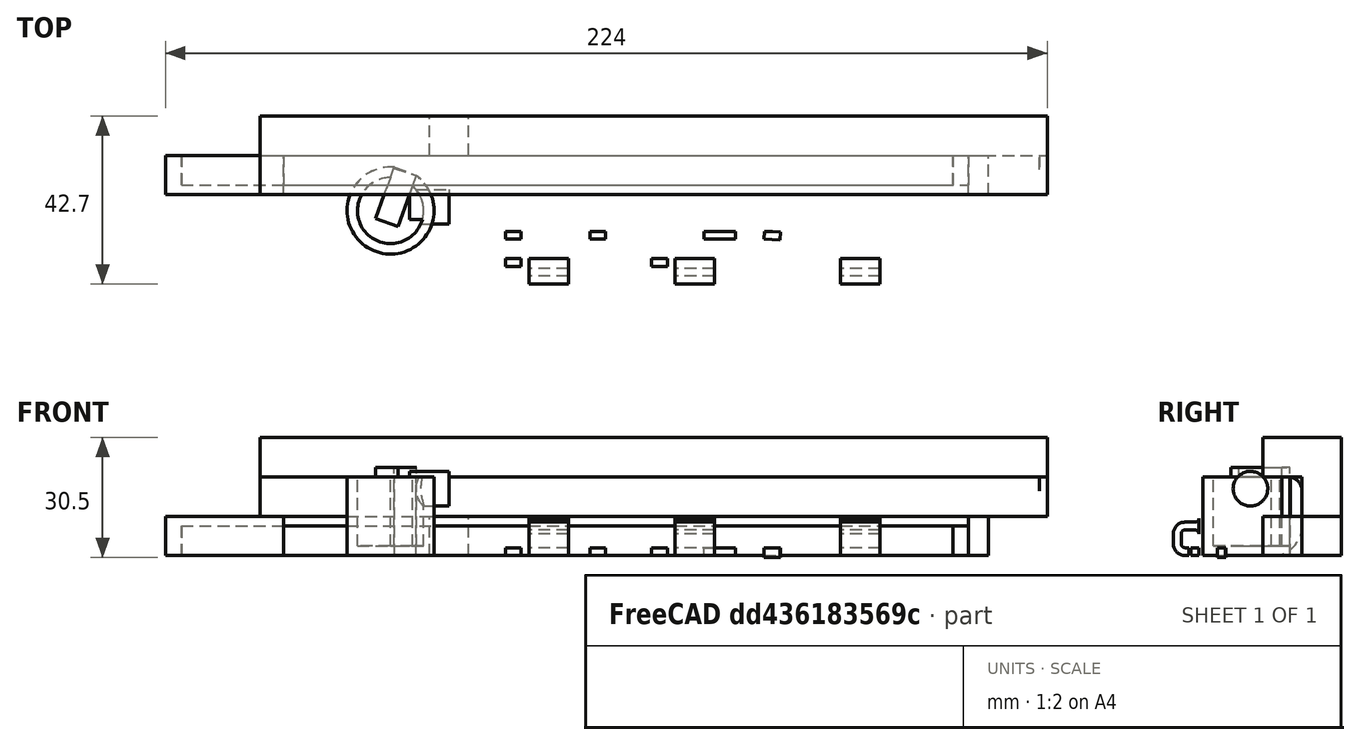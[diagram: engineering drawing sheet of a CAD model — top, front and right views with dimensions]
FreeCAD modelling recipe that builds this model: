
FCSTD DOCUMENT  (FreeCAD 0.19R0.19.2)
Label: v0_73
License: All rights reserved
LicenseURL: http://en.wikipedia.org/wiki/All_rights_reserved
objects: Part::Box×54, Part::Fillet×31, Part::MultiFuse×24, Part::Cut×13, Sketcher::SketchObject×11, Part::Extrusion×9, Part::Cylinder×6, App::MeasureDistance×5, Part::Revolution×1
note: 149 computed .brp shape members not serialized (recipe doc carries the construction recipe); baked Part::Feature solids carry a one-line shape summary decoded from their .brp

FEATURE [Sketcher::SketchObject] Sketch001
  FullyConstrained = true
  sketch-geometry (47):
    g0: Circle CenterX=-129.5 CenterY=-8 CenterZ=0 NormalX=0 NormalY=0 NormalZ=1 AngleXU=0 Radius=1
    g1: Circle CenterX=-129.5 CenterY=-3 CenterZ=0 NormalX=0 NormalY=0 NormalZ=1 AngleXU=0 Radius=1
    g2: Circle CenterX=-124.5 CenterY=-3 CenterZ=0 NormalX=0 NormalY=0 NormalZ=1 AngleXU=0 Radius=1
    g3: BSplineCurve PolesCount=3 KnotsCount=2 Degree=2 IsPeriodic=0
    g4: GeomPoint X=-129.5 Y=-8 Z=0
    g5: GeomPoint X=-124.5 Y=-3 Z=0
    g6: LineSegment StartX=18.6 StartY=-2.9 StartZ=0 EndX=23.6 EndY=-2.9 EndZ=0
    g7: ArcOfCircle CenterX=23.8 CenterY=-14.35 CenterZ=0 NormalX=0 NormalY=0 NormalZ=1 AngleXU=0 Radius=2.3 StartAngle=8e-16 EndAngle=1.5708
    g8: ArcOfCircle CenterX=23.8 CenterY=-18.1 CenterZ=0 NormalX=0 NormalY=0 NormalZ=1 AngleXU=0 Radius=2.3 StartAngle=4.71239 EndAngle=6.28319
    g9: LineSegment StartX=23.8 StartY=-20.4 StartZ=0 EndX=21.1 EndY=-20.4 EndZ=0
    g10: LineSegment StartX=21.1 StartY=-22.9 StartZ=0 EndX=21.1 EndY=-20.4 EndZ=0
    g11: LineSegment StartX=26.1 StartY=-14.35 StartZ=0 EndX=26.1 EndY=-18.1 EndZ=0
    g12: LineSegment StartX=18.6 StartY=-5.40742 StartZ=0 EndX=18.6 EndY=-2.9 EndZ=0
    g13: ArcOfCircle CenterX=18.8 CenterY=-8.1 CenterZ=0 NormalX=0 NormalY=0 NormalZ=1 AngleXU=0 Radius=2.7 StartAngle=1.64494 EndAngle=3.14159
    g14: ArcOfCircle CenterX=18.8 CenterY=-11.85 CenterZ=0 NormalX=0 NormalY=0 NormalZ=1 AngleXU=0 Radius=2.7 StartAngle=3.14159 EndAngle=4.71239
    g15: LineSegment StartX=16.1 StartY=-8.1 StartZ=0 EndX=16.1 EndY=-11.85 EndZ=0
    g16: LineSegment StartX=18.8 StartY=-14.55 StartZ=0 EndX=21.5 EndY=-14.55 EndZ=0
    g17: LineSegment StartX=21.5 StartY=-12.05 StartZ=0 EndX=21.5 EndY=-14.55 EndZ=0
    g18: LineSegment StartX=21.5 StartY=-12.05 StartZ=0 EndX=23.8 EndY=-12.05 EndZ=0
    g19: LineSegment StartX=16.1 StartY=-22.9 StartZ=0 EndX=21.1 EndY=-22.9 EndZ=0
    g20: LineSegment StartX=23.6 StartY=-2.9 StartZ=0 EndX=23.6 EndY=0 EndZ=0
    g21: LineSegment StartX=16.1 StartY=-22.9 StartZ=0 EndX=16.1 EndY=-26.2 EndZ=0
    g22: BSplineCurve PolesCount=3 KnotsCount=2 Degree=2 IsPeriodic=0
    g23: LineSegment StartX=2.6 StartY=-3 StartZ=0 EndX=-124.5 EndY=-3 EndZ=0
    g24: ArcOfCircle CenterX=-134.9 CenterY=-8.6 CenterZ=0 NormalX=0 NormalY=0 NormalZ=1 AngleXU=0 Radius=0.5 StartAngle=4.71238 EndAngle=6.28319
    g25: LineSegment StartX=-141.9 StartY=-9.1 StartZ=0 EndX=-134.9 EndY=-9.1 EndZ=0
    g26: LineSegment StartX=-141.9 StartY=-33.8 StartZ=0 EndX=-141.5 EndY=-33.8 EndZ=0
    g27: LineSegment StartX=-141.9 StartY=-9.1 StartZ=0 EndX=-141.9 EndY=-33.8 EndZ=0
    g28: LineSegment StartX=-134.4 StartY=-8.6 StartZ=0 EndX=-134.4 EndY=0 EndZ=0
    g29: LineSegment StartX=-134.4 StartY=0 StartZ=0 EndX=23.6 EndY=0 EndZ=0
    g30: LineSegment StartX=-133.5 StartY=-26.2 StartZ=0 EndX=16.1 EndY=-26.2 EndZ=0
    g31-g36: Circle x6 (B-spline internal-alignment scaffolding for g37; pole/knot coordinates omitted)
    g37: BSplineCurve PolesCount=6 KnotsCount=4 Degree=3 IsPeriodic=0
    g38-g41: GeomPoint x4 (B-spline internal-alignment scaffolding for g37; pole/knot coordinates omitted)
    g42: BSplineCurve PolesCount=3 KnotsCount=2 Degree=2 IsPeriodic=0
    g43: LineSegment StartX=-129.5 StartY=-8 StartZ=0 EndX=-129.5 EndY=-18.2 EndZ=0
    g44: BSplineCurve PolesCount=3 KnotsCount=2 Degree=2 IsPeriodic=0
    g45: LineSegment StartX=7.6 StartY=-8 StartZ=0 EndX=7.6 EndY=-18.2 EndZ=0
    g46: LineSegment StartX=2.6 StartY=-23.2 StartZ=0 EndX=-124.5 EndY=-23.2 EndZ=0
  constraints (87):
    c: Weight(g0) = 1
    c: Equal(g0,g1)
    c: Equal(g0,g2)
    c: InternalAlignment(g0,g3)
    c: InternalAlignment(g1,g3)
    c: InternalAlignment(g2,g3)
    c: InternalAlignment(g4,g3)
    c: InternalAlignment(g5,g3)
    c: Block(g3)
    c: Block(g8)
    c: Block(g7)
    c: Coincident(g9,g8)
    c: Horizontal(g9)
    c: Vertical(g10)
    c: Coincident(g10,g9)
    c: Coincident(g11,g7)
    c: Coincident(g11,g8)
    c: Vertical(g11)
    c: Vertical(g12)
    c: Block(g12)
    c: Coincident(g6,g12)
    c: Horizontal(g6)
    c: Block(g6)
    c: Coincident(g13,g12)
    c: Block(g14)
    c: Vertical(g15)
    c: Block(g15)
    c: Coincident(g16,g14)
    c: Horizontal(g16)
    c: Vertical(g17)
    c: Coincident(g17,g16)
    c: Block(g17)
    c: Coincident(g18,g7)
    c: Horizontal(g18)
    c: Block(g18)
    c: Coincident(g19,g10)
    c: Horizontal(g19)
    c: Block(g19)
    c: Block(g13)
    c: Coincident(g20,g6)
    c: Vertical(g20)
    c: Vertical(g21)
    c: Block(g21)
    c: Block(g22)
    c: Coincident(g23,g22)
    c: Coincident(g23,g3)
    c: Horizontal(g23)
    c: Block(g24)
    c: Coincident(g25,g24)
    c: Horizontal(g25)
    c: Horizontal(g26)
    c: Block(g26)
    c: Coincident(g27,g25)
    c: Coincident(g27,g26)
    c: Vertical(g27)
    c: Coincident(g28,g24)
    c: Vertical(g28)
    c: Coincident(g29,g28)
    c: Coincident(g29,g20)
    c: Horizontal(g29)
    c: Block(g29)
    c: Block(g25)
    c: Block(g28)
    c: Block(g27)
    c: Coincident(g30,g21)
    c: Horizontal(g30)
    c: Block(g30)
    c: Coincident(g37,g26)
    c: Weight(g31) = 1
    c: Equal(g31, g32-g36) x5
    c: Coincident(g37,g30)
    c: InternalAlignment(g31-g36 -> g37) x6
    c: InternalAlignment(g38-g41 -> g37) x4
    c: Block(g37)
    c: Block(g42)
    c: Coincident(g43,g3)
    c: Coincident(g43,g42)
    c: Vertical(g43)
    c: Distance(g43) = 10.2
    c: Block(g44)
    c: Coincident(g45,g22)
    c: Coincident(g45,g44)
    c: Vertical(g45)
    c: Distance(g45) = 10.2
    c: Coincident(g46,g44)
    c: Coincident(g46,g42)
    c: Horizontal(g46)
FEATURE [Part::Extrusion] Extrude001
  Base = -> Sketch001
  Dir = (0,0,1)
  DirMode = 2
  FaceMakerClass = Part::FaceMakerBullseye
  LengthFwd = 20
  LengthRev = 0
  Solid = true
  Symmetric = false
FEATURE [Sketcher::SketchObject] Sketch004
  FullyConstrained = true
  Placement = pos=(0,0,0) rot=(1,0,0;1.5708rad)
  sketch-geometry (12):
    g0: LineSegment StartX=15.75 StartY=2.5 StartZ=0 EndX=15.75 EndY=0 EndZ=0
    g1: Circle CenterX=15.75 CenterY=2.5 CenterZ=0 NormalX=0 NormalY=0 NormalZ=1 AngleXU=0 Radius=1
    g2: Circle CenterX=10.55 CenterY=2.5 CenterZ=0 NormalX=0 NormalY=0 NormalZ=1 AngleXU=0 Radius=1
    g3: Circle CenterX=10.55 CenterY=8 CenterZ=0 NormalX=0 NormalY=0 NormalZ=1 AngleXU=0 Radius=1
    g4: BSplineCurve PolesCount=3 KnotsCount=2 Degree=2 IsPeriodic=0
    g5: GeomPoint X=15.75 Y=2.5 Z=0
    g6: GeomPoint X=10.55 Y=8 Z=0
    g7: LineSegment StartX=1.9 StartY=8 StartZ=0 EndX=10.55 EndY=8 EndZ=0
    g8: LineSegment StartX=1.9 StartY=-2.4 StartZ=0 EndX=1.9 EndY=8 EndZ=0
    g9: LineSegment StartX=3.30092 StartY=-2.4 StartZ=0 EndX=3.30092 EndY=0 EndZ=0
    g10: LineSegment StartX=15.75 StartY=0 StartZ=0 EndX=3.30092 EndY=0 EndZ=0
    g11: LineSegment StartX=3.30092 StartY=-2.4 StartZ=0 EndX=1.9 EndY=-2.4 EndZ=0
  constraints (26):
    c: Vertical(g0)
    c: Distance(g0) = 2.5
    c: Coincident(g4,g0)
    c: Weight(g1) = 1
    c: Equal(g1,g2)
    c: Equal(g1,g3)
    c: InternalAlignment(g1,g4)
    c: InternalAlignment(g2,g4)
    c: InternalAlignment(g3,g4)
    c: InternalAlignment(g5,g4)
    c: InternalAlignment(g6,g4)
    c: Block(g4)
    c: Coincident(g7,g4)
    c: Horizontal(g7)
    c: Vertical(g8)
    c: Coincident(g8,g7)
    c: Block(g8)
    c: Vertical(g9)
    c: Coincident(g10,g0)
    c: PointOnObject(g10,g-1)
    c: Horizontal(g10)
    c: Coincident(g10,g9)
    c: Block(g9)
    c: Coincident(g11,g9)
    c: Coincident(g11,g8)
    c: Horizontal(g11)
FEATURE [Part::Revolution] Revolve  label="mainScrewStandRevolve"
  Angle = 360
  Axis = (0,0,1)
  Base = (0,0,0)
  FaceMakerClass = Part::FaceMakerBullseye
  Placement = pos=(-101.95,-15.3,0) rot=(0,0,1;0rad)
  Solid = true
  Source = -> Sketch004
  Symmetric = false
FEATURE [Sketcher::SketchObject] Sketch044
  FullyConstrained = true
  MapMode = 4
  Placement = pos=(0,0,0) rot=(0.57735,0.57735,0.57735;2.0944rad)
  sketch-geometry (14):
    g0: LineSegment StartX=6.08745 StartY=-4.11588 StartZ=0 EndX=6.08745 EndY=-2.11589 EndZ=0
    g1: LineSegment StartX=8.08745 StartY=1.38411 StartZ=0 EndX=8.08745 EndY=-1.11589 EndZ=0
    g2: ArcOfCircle CenterX=7.08745 CenterY=-1.11589 CenterZ=0 NormalX=0 NormalY=0 NormalZ=1 AngleXU=0 Radius=1 StartAngle=4.71239 EndAngle=6.28319
    g3: LineSegment StartX=6.08745 StartY=-2.11589 StartZ=0 EndX=7.08745 EndY=-2.11589 EndZ=0
    g4: LineSegment StartX=6.08745 StartY=-4.11588 StartZ=0 EndX=7.08745 EndY=-4.11588 EndZ=0
    g5: ArcOfCircle CenterX=7.08745 CenterY=-1.11589 CenterZ=0 NormalX=0 NormalY=0 NormalZ=1 AngleXU=0 Radius=3 StartAngle=4.71239 EndAngle=6.28319
    g6: ArcOfCircle CenterX=7.08745 CenterY=1.38411 CenterZ=0 NormalX=0 NormalY=0 NormalZ=1 AngleXU=0 Radius=1 StartAngle=5.35e-14 EndAngle=1.5708
    g7: LineSegment StartX=10.0875 StartY=-1.11588 StartZ=0 EndX=10.0875 EndY=1.38411 EndZ=0
    g8: ArcOfCircle CenterX=7.08745 CenterY=1.38411 CenterZ=0 NormalX=0 NormalY=0 NormalZ=1 AngleXU=0 Radius=3 StartAngle=3.57e-14 EndAngle=1.5708
    g9: ArcOfCircle CenterX=4.58745 CenterY=1.38412 CenterZ=0 NormalX=0 NormalY=0 NormalZ=1 AngleXU=0 Radius=1 StartAngle=1.57081 EndAngle=3.14159
    g10: LineSegment StartX=4.58744 StartY=2.38411 StartZ=0 EndX=7.08745 EndY=2.38411 EndZ=0
    g11: LineSegment StartX=4.58745 StartY=4.38411 StartZ=0 EndX=7.08745 EndY=4.38411 EndZ=0
    g12: ArcOfCircle CenterX=4.58745 CenterY=5.38411 CenterZ=0 NormalX=0 NormalY=0 NormalZ=1 AngleXU=0 Radius=1 StartAngle=3.14159 EndAngle=4.71239
    g13: LineSegment StartX=3.58745 StartY=5.38411 StartZ=0 EndX=3.58745 EndY=1.38411 EndZ=0
  constraints (33):
    c: Vertical(g0)
    c: Block(g0)
    c: Block(g1)
    c: Coincident(g2,g1)
    c: Coincident(g3,g0)
    c: Coincident(g3,g2)
    c: Horizontal(g3)
    c: Block(g2)
    c: Coincident(g4,g0)
    c: Horizontal(g4)
    c: Coincident(g5,g2)
    c: Block(g5)
    c: Block(g4)
    c: Coincident(g6,g1)
    c: Block(g6)
    c: Coincident(g7,g5)
    c: Vertical(g7)
    c: Coincident(g8,g6)
    c: Block(g8)
    c: Block(g7)
    c: Coincident(g10,g9)
    c: Coincident(g10,g6)
    c: Horizontal(g10)
    c: Block(g10)
    c: Block(g9)
    c: Coincident(g11,g8)
    c: Horizontal(g11)
    c: Block(g12)
    c: Block(g11)
    c: Coincident(g13,g12)
    c: Coincident(g13,g9)
    c: Vertical(g13)
    c: Tangent(g13,g9)
FEATURE [Sketcher::SketchObject] Sketch045
  FullyConstrained = true
  MapMode = 4
  Placement = pos=(0,0,0) rot=(0.57735,0.57735,0.57735;2.0944rad)
  sketch-geometry (14):
    g0: LineSegment StartX=6.08745 StartY=-4.11588 StartZ=0 EndX=6.08745 EndY=-2.11589 EndZ=0
    g1: LineSegment StartX=8.08745 StartY=1.38411 StartZ=0 EndX=8.08745 EndY=-1.11589 EndZ=0
    g2: ArcOfCircle CenterX=7.08745 CenterY=-1.11589 CenterZ=0 NormalX=0 NormalY=0 NormalZ=1 AngleXU=0 Radius=1 StartAngle=4.71239 EndAngle=6.28319
    g3: LineSegment StartX=6.08745 StartY=-2.11589 StartZ=0 EndX=7.08745 EndY=-2.11589 EndZ=0
    g4: LineSegment StartX=6.08745 StartY=-4.11588 StartZ=0 EndX=7.08745 EndY=-4.11588 EndZ=0
    g5: ArcOfCircle CenterX=7.08745 CenterY=-1.11589 CenterZ=0 NormalX=0 NormalY=0 NormalZ=1 AngleXU=0 Radius=3 StartAngle=4.71239 EndAngle=6.28319
    g6: ArcOfCircle CenterX=7.08745 CenterY=1.38411 CenterZ=0 NormalX=0 NormalY=0 NormalZ=1 AngleXU=0 Radius=1 StartAngle=5.35e-14 EndAngle=1.5708
    g7: LineSegment StartX=10.0875 StartY=-1.11588 StartZ=0 EndX=10.0875 EndY=1.38411 EndZ=0
    g8: ArcOfCircle CenterX=7.08745 CenterY=1.38411 CenterZ=0 NormalX=0 NormalY=0 NormalZ=1 AngleXU=0 Radius=3 StartAngle=3.57e-14 EndAngle=1.5708
    g9: ArcOfCircle CenterX=4.58745 CenterY=1.38412 CenterZ=0 NormalX=0 NormalY=0 NormalZ=1 AngleXU=0 Radius=1 StartAngle=1.57081 EndAngle=3.14159
    g10: LineSegment StartX=4.58744 StartY=2.38411 StartZ=0 EndX=7.08745 EndY=2.38411 EndZ=0
    g11: LineSegment StartX=4.58745 StartY=4.38411 StartZ=0 EndX=7.08745 EndY=4.38411 EndZ=0
    g12: ArcOfCircle CenterX=4.58745 CenterY=5.38411 CenterZ=0 NormalX=0 NormalY=0 NormalZ=1 AngleXU=0 Radius=1 StartAngle=3.14159 EndAngle=4.71239
    g13: LineSegment StartX=3.58745 StartY=5.38411 StartZ=0 EndX=3.58745 EndY=1.38411 EndZ=0
  constraints (33):
    c: Vertical(g0)
    c: Block(g0)
    c: Block(g1)
    c: Coincident(g2,g1)
    c: Coincident(g3,g0)
    c: Coincident(g3,g2)
    c: Horizontal(g3)
    c: Block(g2)
    c: Coincident(g4,g0)
    c: Horizontal(g4)
    c: Coincident(g5,g2)
    c: Block(g5)
    c: Block(g4)
    c: Coincident(g6,g1)
    c: Block(g6)
    c: Coincident(g7,g5)
    c: Vertical(g7)
    c: Coincident(g8,g6)
    c: Block(g8)
    c: Block(g7)
    c: Coincident(g10,g9)
    c: Coincident(g10,g6)
    c: Horizontal(g10)
    c: Block(g10)
    c: Block(g9)
    c: Coincident(g11,g8)
    c: Horizontal(g11)
    c: Block(g12)
    c: Block(g11)
    c: Coincident(g13,g12)
    c: Coincident(g13,g9)
    c: Vertical(g13)
    c: Tangent(g13,g9)
FEATURE [Part::Extrusion] Extrude040
  Base = -> Sketch045
  Dir = (1,0,0)
  DirMode = 2
  FaceMakerClass = Part::FaceMakerBullseye
  LengthFwd = 10
  LengthRev = 0
  Placement = pos=(-71.7,-22.61,4.115) rot=(0,0,1;3.14159rad)
  Solid = true
  Symmetric = false
FEATURE [Part::Box] Box017  label="Cube017"
  AttacherType = Attacher::AttachEngine3D
  Height = 2
  Length = 2
  Placement = pos=(-85.7,-21.3,0) rot=(0,0,1;0rad)
  Width = 2
FEATURE [Part::Box] Box018  label="Cube018"
  AttacherType = Attacher::AttachEngine3D
  Height = 2
  Length = 2
  Placement = pos=(-87.7,-21.3,0) rot=(0,0,1;0rad)
  Width = 2
FEATURE [Part::MultiFuse] Fusion
  Placement = pos=(0,-6.9,0) rot=(0,0,1;0rad)
  Shapes = -> [Box017,Box018]
FEATURE [Part::Box] Box021  label="Cube021"
  AttacherType = Attacher::AttachEngine3D
  Height = 2
  Length = 2
  Placement = pos=(-85.7,-21.3,0) rot=(0,0,1;0rad)
  Width = 2
FEATURE [Part::Box] Box022  label="Cube022"
  AttacherType = Attacher::AttachEngine3D
  Height = 2
  Length = 2
  Placement = pos=(-87.7,-21.3,0) rot=(0,0,1;0rad)
  Width = 2
FEATURE [Part::Box] Box023  label="Cube023"
  AttacherType = Attacher::AttachEngine3D
  Height = 2
  Length = 2
  Placement = pos=(-85.7,-21.3,0) rot=(0,0,1;0rad)
  Width = 2
FEATURE [Part::Box] Box024  label="Cube024"
  AttacherType = Attacher::AttachEngine3D
  Height = 2
  Length = 2
  Placement = pos=(-87.7,-21.3,0) rot=(0,0,1;0rad)
  Width = 2
FEATURE [Part::Box] Box026  label="Cube026"
  AttacherType = Attacher::AttachEngine3D
  Height = 2
  Length = 2
  Placement = pos=(-87.7,-21.3,0) rot=(0,0,1;0rad)
  Width = 2
FEATURE [Part::Box] Box  label="Cube"
  AttacherType = Attacher::AttachEngine3D
  Height = 10
  Length = 10
  Placement = pos=(-107,0,0) rot=(0,0,1;0rad)
  Width = 10
FEATURE [Sketcher::SketchObject] Sketch046
  FullyConstrained = true
  MapMode = 4
  Placement = pos=(0,0,0) rot=(0.57735,0.57735,0.57735;2.0944rad)
  sketch-geometry (14):
    g0: LineSegment StartX=6.08745 StartY=-4.11588 StartZ=0 EndX=6.08745 EndY=-2.11589 EndZ=0
    g1: LineSegment StartX=8.08745 StartY=1.38411 StartZ=0 EndX=8.08745 EndY=-1.11589 EndZ=0
    g2: ArcOfCircle CenterX=7.08745 CenterY=-1.11589 CenterZ=0 NormalX=0 NormalY=0 NormalZ=1 AngleXU=0 Radius=1 StartAngle=4.71239 EndAngle=6.28319
    g3: LineSegment StartX=6.08745 StartY=-2.11589 StartZ=0 EndX=7.08745 EndY=-2.11589 EndZ=0
    g4: LineSegment StartX=6.08745 StartY=-4.11588 StartZ=0 EndX=7.08745 EndY=-4.11588 EndZ=0
    g5: ArcOfCircle CenterX=7.08745 CenterY=-1.11589 CenterZ=0 NormalX=0 NormalY=0 NormalZ=1 AngleXU=0 Radius=3 StartAngle=4.71239 EndAngle=6.28319
    g6: ArcOfCircle CenterX=7.08745 CenterY=1.38411 CenterZ=0 NormalX=0 NormalY=0 NormalZ=1 AngleXU=0 Radius=1 StartAngle=5.35e-14 EndAngle=1.5708
    g7: LineSegment StartX=10.0875 StartY=-1.11588 StartZ=0 EndX=10.0875 EndY=1.38411 EndZ=0
    g8: ArcOfCircle CenterX=7.08745 CenterY=1.38411 CenterZ=0 NormalX=0 NormalY=0 NormalZ=1 AngleXU=0 Radius=3 StartAngle=3.57e-14 EndAngle=1.5708
    g9: ArcOfCircle CenterX=4.58745 CenterY=1.38412 CenterZ=0 NormalX=0 NormalY=0 NormalZ=1 AngleXU=0 Radius=1 StartAngle=1.57081 EndAngle=3.14159
    g10: LineSegment StartX=4.58744 StartY=2.38411 StartZ=0 EndX=7.08745 EndY=2.38411 EndZ=0
    g11: LineSegment StartX=4.58745 StartY=4.38411 StartZ=0 EndX=7.08745 EndY=4.38411 EndZ=0
    g12: ArcOfCircle CenterX=4.58745 CenterY=5.38411 CenterZ=0 NormalX=0 NormalY=0 NormalZ=1 AngleXU=0 Radius=1 StartAngle=3.14159 EndAngle=4.71239
    g13: LineSegment StartX=3.58745 StartY=5.38411 StartZ=0 EndX=3.58745 EndY=1.38411 EndZ=0
  constraints (33):
    c: Vertical(g0)
    c: Block(g0)
    c: Block(g1)
    c: Coincident(g2,g1)
    c: Coincident(g3,g0)
    c: Coincident(g3,g2)
    c: Horizontal(g3)
    c: Block(g2)
    c: Coincident(g4,g0)
    c: Horizontal(g4)
    c: Coincident(g5,g2)
    c: Block(g5)
    c: Block(g4)
    c: Coincident(g6,g1)
    c: Block(g6)
    c: Coincident(g7,g5)
    c: Vertical(g7)
    c: Coincident(g8,g6)
    c: Block(g8)
    c: Block(g7)
    c: Coincident(g10,g9)
    c: Coincident(g10,g6)
    c: Horizontal(g10)
    c: Block(g10)
    c: Block(g9)
    c: Coincident(g11,g8)
    c: Horizontal(g11)
    c: Block(g12)
    c: Block(g11)
    c: Coincident(g13,g12)
    c: Coincident(g13,g9)
    c: Vertical(g13)
    c: Tangent(g13,g9)
FEATURE [Part::Extrusion] Extrude041
  Base = -> Sketch046
  Dir = (1,0,0)
  DirMode = 2
  FaceMakerClass = Part::FaceMakerBullseye
  LengthFwd = 10
  LengthRev = 0
  Placement = pos=(7.5,-22.61,4.115) rot=(0,0,1;3.14159rad)
  Solid = true
  Symmetric = false
FEATURE [Part::Box] Box027  label="Cube027"
  AttacherType = Attacher::AttachEngine3D
  Height = 2
  Length = 2
  Placement = pos=(-85.7,-21.3,0) rot=(0,0,1;0rad)
  Width = 2
FEATURE [Part::Box] Box028  label="Cube028"
  AttacherType = Attacher::AttachEngine3D
  Height = 2
  Length = 2
  Placement = pos=(-87.7,-21.3,0) rot=(0,0,1;0rad)
  Width = 2
FEATURE [Part::MultiFuse] Fusion009
  Placement = pos=(21.5,0,0) rot=(0,0,1;0rad)
  Shapes = -> [Box027,Box028]
FEATURE [Part::Box] Box029  label="Cube029"
  AttacherType = Attacher::AttachEngine3D
  Height = 2
  Length = 2
  Placement = pos=(-87.7,-21.3,0) rot=(0,0,1;0rad)
  Width = 2
FEATURE [Part::Box] Box030  label="Cube030"
  AttacherType = Attacher::AttachEngine3D
  Height = 2
  Length = 2
  Placement = pos=(-85.7,-21.3,0) rot=(0,0,1;0rad)
  Width = 2
FEATURE [Part::MultiFuse] Fusion010
  Shapes = -> [Box030,Box029]
FEATURE [Part::Box] Box032  label="Cube032"
  AttacherType = Attacher::AttachEngine3D
  Height = 2
  Length = 2
  Placement = pos=(-85.7,-21.3,0) rot=(0,0,1;0rad)
  Width = 2
FEATURE [Part::Box] Box033  label="Cube033"
  AttacherType = Attacher::AttachEngine3D
  Height = 2
  Length = 2
  Placement = pos=(-87.7,-21.3,0) rot=(0,0,1;0rad)
  Width = 2
FEATURE [Part::MultiFuse] Fusion011
  Shapes = -> [Box032,Box033]
FEATURE [Part::Box] Box042  label="Cube042"
  AttacherType = Attacher::AttachEngine3D
  Height = 2
  Length = 2
  Placement = pos=(-87.7,-21.3,0) rot=(0,0,1;0rad)
  Width = 2
FEATURE [Part::Box] Box043  label="Cube043"
  AttacherType = Attacher::AttachEngine3D
  Height = 2
  Length = 2
  Placement = pos=(-85.7,-21.3,0) rot=(0,0,1;0rad)
  Width = 2
FEATURE [Part::MultiFuse] Fusion019
  Placement = pos=(37.15,-6.9,0) rot=(0,0,1;0rad)
  Shapes = -> [Box043,Box042]
FEATURE [Part::Box] Box044  label="Cube044"
  AttacherType = Attacher::AttachEngine3D
  Height = 2
  Length = 2
  Placement = pos=(-87.7,-21.3,0) rot=(0,0,1;0rad)
  Width = 2
FEATURE [Part::Box] Box045  label="Cube045"
  AttacherType = Attacher::AttachEngine3D
  Height = 2
  Length = 2
  Placement = pos=(-85.7,-21.3,0) rot=(0,0,1;0rad)
  Width = 2
FEATURE [Part::MultiFuse] Fusion020
  Placement = pos=(69.3,0,0) rot=(0,0,1;0rad)
  Shapes = -> [Box045,Box044]
FEATURE [Part::Box] Box046  label="Cube046"
  AttacherType = Attacher::AttachEngine3D
  Height = 2
  Length = 2
  Placement = pos=(-87.7,-21.3,0) rot=(0,0,1;0rad)
  Width = 2
FEATURE [Part::Box] Box047  label="Cube047"
  AttacherType = Attacher::AttachEngine3D
  Height = 2
  Length = 2
  Placement = pos=(-85.7,-21.3,0) rot=(0,0,1;0rad)
  Width = 2
FEATURE [Part::MultiFuse] Fusion021
  Placement = pos=(73.3,0,0) rot=(0,0,1;0rad)
  Shapes = -> [Box047,Box046]
FEATURE [Part::Box] Box048  label="Cube048"
  AttacherType = Attacher::AttachEngine3D
  Height = 2
  Length = 2
  Placement = pos=(-87.7,-21.3,0) rot=(0,0,1;0rad)
  Width = 2
FEATURE [Part::Box] Box049  label="Cube049"
  AttacherType = Attacher::AttachEngine3D
  Height = 2
  Length = 2
  Placement = pos=(-85.7,-21.3,0) rot=(0,0,1;0rad)
  Width = 2
FEATURE [Part::MultiFuse] Fusion022
  Placement = pos=(64.3,0,0) rot=(0,0,1;0rad)
  Shapes = -> [Box049,Box048]
FEATURE [Part::MultiFuse] Fusion025
  Shapes = -> [Box021,Box022,Box023,Box024,Box026]
FEATURE [Part::Box] Box005  label="Cube005"
  AttacherType = Attacher::AttachEngine3D
  Height = 10
  Length = 198
  Placement = pos=(-30,0,0) rot=(0,0,1;0rad)
  Width = 10
FEATURE [Part::Box] Box004  label="Cube004"
  AttacherType = Attacher::AttachEngine3D
  Height = 10
  Length = 200
  Placement = pos=(-30,0,0) rot=(0,0,1;0rad)
  Width = 10
FEATURE [Part::Fillet] Fillet020
  Base = -> Box004
  Edges = 1 edges r=3.6: [Edge12]
FEATURE [Sketcher::SketchObject] Sketch
  FullyConstrained = true
  sketch-geometry (35):
    g0: Circle CenterX=-101.95 CenterY=-14.3 CenterZ=0 NormalX=0 NormalY=0 NormalZ=1 AngleXU=0 Radius=3.25
    g1: LineSegment StartX=16.1 StartY=-26.2 StartZ=0 EndX=16.1 EndY=-22.9 EndZ=0
    g2: ArcOfCircle CenterX=23.8 CenterY=-14.35 CenterZ=0 NormalX=0 NormalY=0 NormalZ=1 AngleXU=0 Radius=2.3 StartAngle=8e-16 EndAngle=1.5708
    g3: LineSegment StartX=18.6 StartY=-5.40742 StartZ=0 EndX=18.6 EndY=-2.9 EndZ=0
    g4: LineSegment StartX=18.6 StartY=-2.9 StartZ=0 EndX=23.6 EndY=-2.9 EndZ=0
    g5: LineSegment StartX=23.6 StartY=-2.9 StartZ=0 EndX=23.6 EndY=2.58e-14 EndZ=0
    g6: LineSegment StartX=18.8 StartY=-14.55 StartZ=0 EndX=21.5 EndY=-14.55 EndZ=0
    g7: LineSegment StartX=21.5 StartY=-12.05 StartZ=0 EndX=21.5 EndY=-14.55 EndZ=0
    g8: LineSegment StartX=21.5 StartY=-12.05 StartZ=0 EndX=23.8 EndY=-12.05 EndZ=0
    g9: ArcOfCircle CenterX=23.8 CenterY=-18.1 CenterZ=0 NormalX=0 NormalY=0 NormalZ=1 AngleXU=0 Radius=2.3 StartAngle=4.71239 EndAngle=6.28319
    g10: LineSegment StartX=23.8 StartY=-20.4 StartZ=0 EndX=21.1 EndY=-20.4 EndZ=0
    g11: LineSegment StartX=26.1 StartY=-14.35 StartZ=0 EndX=26.1 EndY=-18.1 EndZ=0
    g12: ArcOfCircle CenterX=18.8 CenterY=-8.1 CenterZ=0 NormalX=0 NormalY=0 NormalZ=1 AngleXU=0 Radius=2.7 StartAngle=1.64494 EndAngle=3.14159
    g13: ArcOfCircle CenterX=18.8 CenterY=-11.85 CenterZ=0 NormalX=0 NormalY=0 NormalZ=1 AngleXU=0 Radius=2.7 StartAngle=3.14159 EndAngle=4.71239
    g14: LineSegment StartX=16.1 StartY=-8.1 StartZ=0 EndX=16.1 EndY=-11.85 EndZ=0
    g15: LineSegment StartX=21.1 StartY=-22.9 StartZ=0 EndX=21.1 EndY=-20.4 EndZ=0
    g16: LineSegment StartX=16.1 StartY=-22.9 StartZ=0 EndX=21.1 EndY=-22.9 EndZ=0
    g17: LineSegment StartX=23.6 StartY=2.58e-14 StartZ=0 EndX=-134.4 EndY=2.58e-14 EndZ=0
    g18: LineSegment StartX=-134.4 StartY=2.59e-14 StartZ=0 EndX=-134.4 EndY=-8.6 EndZ=0
    g19: ArcOfCircle CenterX=-134.9 CenterY=-8.6 CenterZ=0 NormalX=0 NormalY=0 NormalZ=1 AngleXU=0 Radius=0.5 StartAngle=4.71238 EndAngle=6.28319
    g20: LineSegment StartX=-134.9 StartY=-9.1 StartZ=0 EndX=-141.9 EndY=-9.1 EndZ=0
    g21: LineSegment StartX=-141.9 StartY=-9.1 StartZ=0 EndX=-141.9 EndY=-33.8 EndZ=0
    g22: LineSegment StartX=-141.9 StartY=-33.8 StartZ=0 EndX=-141.5 EndY=-33.8 EndZ=0
    g23: LineSegment StartX=-133.5 StartY=-26.2 StartZ=0 EndX=16.1 EndY=-26.2 EndZ=0
    g24-g29: Circle x6 (B-spline internal-alignment scaffolding for g30; pole/knot coordinates omitted)
    g30: BSplineCurve PolesCount=6 KnotsCount=4 Degree=3 IsPeriodic=0
    g31-g34: GeomPoint x4 (B-spline internal-alignment scaffolding for g30; pole/knot coordinates omitted)
  constraints (61):
    c: Block(g0)
    c: Vertical(g1)
    c: Distance(g1) = 3.3
    c: Block(g9)
    c: Block(g2)
    c: Coincident(g10,g9)
    c: Horizontal(g10)
    c: Vertical(g15)
    c: Coincident(g15,g10)
    c: Coincident(g11,g2)
    c: Coincident(g11,g9)
    c: Vertical(g11)
    c: Vertical(g3)
    c: Block(g3)
    c: Coincident(g4,g3)
    c: Horizontal(g4)
    c: Vertical(g5)
    c: Block(g5)
    c: Block(g4)
    c: Coincident(g12,g3)
    c: Block(g13)
    c: Coincident(g14,g12)
    c: Vertical(g14)
    c: Block(g14)
    c: Coincident(g6,g13)
    c: Horizontal(g6)
    c: Vertical(g7)
    c: Coincident(g7,g6)
    c: Block(g7)
    c: Coincident(g8,g2)
    c: Horizontal(g8)
    c: Block(g8)
    c: Coincident(g16,g15)
    c: Horizontal(g16)
    c: Block(g16)
    c: Block(g12)
    c: Coincident(g16,g1)
    c: Coincident(g17,g5)
    c: Horizontal(g17)
    c: Vertical(g18)
    c: Horizontal(g20)
    c: Coincident(g19,g18)
    c: Coincident(g19,g20)
    c: Block(g19)
    c: Coincident(g21,g20)
    c: Vertical(g21)
    c: Block(g21)
    c: Coincident(g22,g21)
    c: Horizontal(g22)
    c: Block(g22)
    c: Block(g18)
    c: Coincident(g18,g17)
    c: Coincident(g23,g1)
    c: Horizontal(g23)
    c: Distance(g23) = 149.6
    c: Coincident(g30,g22)
    c: Weight(g24) = 1
    c: Equal(g24, g25-g29) x5
    c: InternalAlignment(g24-g29 -> g30) x6
    c: InternalAlignment(g31-g34 -> g30) x4
    c: Block(g30)
FEATURE [Part::Extrusion] Extrude
  Base = -> Sketch
  Dir = (0,0,1)
  DirMode = 2
  FaceMakerClass = Part::FaceMakerBullseye
  LengthFwd = 2.4
  LengthRev = 0
  Solid = true
  Symmetric = false
FEATURE [Part::Box] Box051  label="Cube051"
  AttacherType = Attacher::AttachEngine3D
  Height = 10
  Length = 198
  Placement = pos=(-30,0,0) rot=(0,0,1;0rad)
  Width = 10
FEATURE [Part::Box] Box052  label="Cube052"
  AttacherType = Attacher::AttachEngine3D
  Height = 5
  Length = 200
  Placement = pos=(-30,6.4,10) rot=(1,0,0;0rad)
  Width = 5
FEATURE [Part::Box] Box053  label="Cube053"
  AttacherType = Attacher::AttachEngine3D
  Height = 5
  Length = 200
  Placement = pos=(-30,6.4,10) rot=(1,0,0;0.872665rad)
  Width = 5
FEATURE [Part::Box] Box054  label="Cube054"
  AttacherType = Attacher::AttachEngine3D
  Height = 10
  Length = 200
  Placement = pos=(-30,0,0) rot=(0,0,1;0rad)
  Width = 10
FEATURE [Part::Fillet] Fillet021
  Base = -> Box054
  Edges = 1 edges r=3.6: [Edge12]
FEATURE [Part::Cut] Cut015
  Base = -> Box051
  Tool = -> Fillet021
FEATURE [Part::MultiFuse] Fusion033  label="removeFromMainFusion014"
  Placement = pos=(-120,-10,10) rot=(0,0,1;0rad)
  Shapes = -> [Box053,Box052,Cut015]
FEATURE [Part::Box] Box055  label="Cube055"
  AttacherType = Attacher::AttachEngine3D
  Height = 10
  Length = 190
  Placement = pos=(-30,0,0) rot=(0,0,1;0rad)
  Width = 10
FEATURE [Part::Box] Box056  label="Cube056"
  AttacherType = Attacher::AttachEngine3D
  Height = 10
  Length = 190
  Placement = pos=(-35,0,0) rot=(0,0,1;0rad)
  Width = 10
FEATURE [Part::Fillet] Fillet022
  Base = -> Box055
  Edges = 1 edges r=7.5: [Edge11]
FEATURE [Part::Cut] Cut014  label="filletMain001"
  Base = -> Box056
  Placement = pos=(-120,-10,0) rot=(0,0,1;0rad)
  Tool = -> Fillet022
FEATURE [Part::MultiFuse] Fusion032  label="removeFromMain001"
  Shapes = -> [Fusion033,Cut014]
FEATURE [Part::Cut] Cut017
  Base = -> Extrude
  Tool = -> Fusion032
FEATURE [Part::Box] Box063  label="Cube063"
  AttacherType = Attacher::AttachEngine3D
  Height = 10
  Length = 198
  Placement = pos=(-30,0,0) rot=(0,0,1;0rad)
  Width = 10
FEATURE [Part::Box] Box064  label="Cube064"
  AttacherType = Attacher::AttachEngine3D
  Height = 5
  Length = 200
  Placement = pos=(-30,6.4,10) rot=(1,0,0;0rad)
  Width = 5
FEATURE [Part::Box] Box065  label="Cube065"
  AttacherType = Attacher::AttachEngine3D
  Height = 5
  Length = 200
  Placement = pos=(-30,6.4,10) rot=(1,0,0;0.872665rad)
  Width = 5
FEATURE [Part::Box] Box066  label="Cube066"
  AttacherType = Attacher::AttachEngine3D
  Height = 10
  Length = 200
  Placement = pos=(-30,0,0) rot=(0,0,1;0rad)
  Width = 10
FEATURE [Part::Fillet] Fillet023
  Base = -> Box066
  Edges = 1 edges r=3.6: [Edge12]
FEATURE [Part::Cut] Cut018
  Base = -> Box063
  Tool = -> Fillet023
FEATURE [Part::MultiFuse] Fusion035  label="removeFromMainFusion015"
  Placement = pos=(-120,-10,10) rot=(0,0,1;0rad)
  Shapes = -> [Box065,Box064,Cut018]
FEATURE [Part::Box] Box067  label="Cube067"
  AttacherType = Attacher::AttachEngine3D
  Height = 10
  Length = 190
  Placement = pos=(-30,0,0) rot=(0,0,1;0rad)
  Width = 10
FEATURE [Part::Fillet] Fillet024
  Base = -> Box067
  Edges = 1 edges r=7.5: [Edge11]
FEATURE [Part::Box] Box068  label="Cube068"
  AttacherType = Attacher::AttachEngine3D
  Height = 10
  Length = 190
  Placement = pos=(-35,0,0) rot=(0,0,1;0rad)
  Width = 10
FEATURE [Part::Cut] Cut019  label="filletMain002"
  Base = -> Box068
  Placement = pos=(-120,-10,0) rot=(0,0,1;0rad)
  Tool = -> Fillet024
FEATURE [Part::MultiFuse] Fusion036  label="removeFromMain002"
  Shapes = -> [Fusion035,Cut019]
FEATURE [Part::Box] Box069  label="Cube069"
  AttacherType = Attacher::AttachEngine3D
  Height = 20
  Length = 10
  Placement = pos=(-144.4,-8,0) rot=(0,0,1;0rad)
  Width = 10
FEATURE [Part::Box] Box070  label="Cube070"
  AttacherType = Attacher::AttachEngine3D
  Height = 20
  Length = 30
  Placement = pos=(-120,0,0) rot=(0,0,1;0rad)
  Width = 20
FEATURE [Part::MultiFuse] Fusion037  label="removeFromIntegrityIncreaserFusion037"
  Shapes = -> [Box069,Box070,Fusion036]
FEATURE [Sketcher::SketchObject] Sketch047
  FullyConstrained = true
  sketch-geometry (4):
    g0: LineSegment StartX=20.5 StartY=-1.82002 StartZ=0 EndX=20.5 EndY=-36 EndZ=0
    g1: LineSegment StartX=32.7 StartY=-36 StartZ=0 EndX=32.7 EndY=-1.82002 EndZ=0
    g2: LineSegment StartX=20.5 StartY=-1.82002 StartZ=0 EndX=32.7 EndY=-1.82002 EndZ=0
    g3: LineSegment StartX=20.5 StartY=-36 StartZ=0 EndX=32.7 EndY=-36 EndZ=0
  constraints (12):
    c: Vertical(g0)
    c: Distance(g0) = 34.18
    c: Vertical(g1)
    c: Block(g0)
    c: Coincident(g2,g0)
    c: Horizontal(g2)
    c: Coincident(g2,g1)
    c: Block(g2)
    c: Block(g1)
    c: Coincident(g3,g0)
    c: Coincident(g3,g1)
    c: Horizontal(g3)
FEATURE [Part::MultiFuse] Fusion038
  Placement = pos=(-18.8,0,0) rot=(0,0,1;0rad)
  Shapes = -> [Fusion020,Fusion021]
FEATURE [Part::Box] Box071  label="Cube071"
  AttacherType = Attacher::AttachEngine3D
  Height = 2
  Length = 2
  Placement = pos=(-87.7,-21.3,0) rot=(0,0,1;0rad)
  Width = 2
FEATURE [Part::Box] Box072  label="Cube072"
  AttacherType = Attacher::AttachEngine3D
  Height = 2
  Length = 2
  Placement = pos=(-85.7,-21.3,0) rot=(0,0,1;0rad)
  Width = 2
FEATURE [Part::MultiFuse] Fusion039
  Placement = pos=(64.3,0,-0.5) rot=(0,0,1;0rad)
  Shapes = -> [Box072,Box071]
FEATURE [Part::MultiFuse] Fusion040  label="removeFromHook"
  Placement = pos=(2.4,-1.09,0) rot=(0,0,-1;0.045379rad)
  Shapes = -> [Fusion022,Fusion039]
FEATURE [Part::Cut] Cut021
  Base = -> Box005
  Tool = -> Fillet020
FEATURE [Part::Box] Box073  label="Cube073"
  AttacherType = Attacher::AttachEngine3D
  Height = 10
  Length = 200
  Placement = pos=(-30,10,0) rot=(0,0,1;0rad)
  Width = 10
FEATURE [Part::Box] Box074  label="Cube074"
  AttacherType = Attacher::AttachEngine3D
  Height = 10
  Length = 200
  Placement = pos=(-30,0,10) rot=(0,0,1;0rad)
  Width = 10
FEATURE [Part::Box] Box075  label="Cube075"
  AttacherType = Attacher::AttachEngine3D
  Height = 10
  Length = 200
  Placement = pos=(-30,10,10) rot=(0,0,1;0rad)
  Width = 10
FEATURE [Part::MultiFuse] Fusion043  label="removeFromMainFusion043"
  Placement = pos=(-120,-10,10) rot=(0,0,1;0rad)
  Shapes = -> [Cut021,Box074,Box073,Box075]
FEATURE [Part::Box] Box076  label="Cube076"
  AttacherType = Attacher::AttachEngine3D
  Height = 10
  Length = 200
  Placement = pos=(-160,0,0) rot=(0,0,1;0rad)
  Width = 10
FEATURE [Part::Box] Box077  label="Cube077"
  AttacherType = Attacher::AttachEngine3D
  Height = 10
  Length = 170
  Placement = pos=(-130,0,0) rot=(0,0,1;0rad)
  Width = 10
FEATURE [Part::Fillet] Fillet028
  Base = -> Box077
  Edges = 1 edges r=7.5: [Edge11]
FEATURE [Part::Cut] Cut024
  Base = -> Box076
  Placement = pos=(-14,-10,0) rot=(0,0,1;0rad)
  Tool = -> Fillet028
FEATURE [Part::Box] Box078  label="Cube078"
  AttacherType = Attacher::AttachEngine3D
  Height = 10
  Length = 200
  Width = 10
FEATURE [Part::Box] Box079  label="Cube079"
  AttacherType = Attacher::AttachEngine3D
  Height = 10
  Length = 205
  Placement = pos=(10,0,0) rot=(0,0,1;0rad)
  Width = 10
FEATURE [Part::Fillet] Fillet029
  Base = -> Box078
  Edges = 1 edges r=7.5: [Edge11]
  Placement = pos=(10,0,0) rot=(0,0,1;0rad)
FEATURE [Part::Cut] Cut025  label="removeFromMainCut025"
  Base = -> Box079
  Placement = pos=(-180,-10,0) rot=(0,0,1;0rad)
  Tool = -> Fillet029
FEATURE [Part::Cylinder] Cylinder001
  Angle = 360
  AttacherType = Attacher::AttachEngine3D
  Height = 10
  Placement = pos=(-36.2,-2,12) rot=(0,1,0;1.5708rad)
  Radius = 2
FEATURE [App::MeasureDistance] Distance  label="Distance: 4.02 mm"
  Distance = 4.02
  P1 = (-33.21,5.8978,9.90268)
  P2 = (-29.19,5.8978,9.90268)
FEATURE [Part::Fillet] Fillet030
  Base = -> Cylinder001
  Edges = 1 edges r=1.8: [Edge3]
FEATURE [Part::Fillet] Fillet031
  Base = -> Fillet030
  Edges = 1 edges r=1.8: [Edge2]
FEATURE [Part::Cylinder] Cylinder003
  Angle = 360
  AttacherType = Attacher::AttachEngine3D
  Height = 10
  Placement = pos=(-36.2,-2,12) rot=(0,1,0;1.5708rad)
  Radius = 2
FEATURE [Part::Fillet] Fillet035
  Base = -> Cylinder003
  Edges = 1 edges r=1.8: [Edge3]
FEATURE [Part::Fillet] Fillet036
  Base = -> Fillet035
  Edges = 1 edges r=1.8: [Edge2]
  Placement = pos=(-12.8,0,0) rot=(0,0,1;0rad)
FEATURE [Part::Cylinder] Cylinder004
  Angle = 360
  AttacherType = Attacher::AttachEngine3D
  Height = 10
  Placement = pos=(-36.2,-2,12) rot=(0,1,0;1.5708rad)
  Radius = 2
FEATURE [Part::Fillet] Fillet038
  Base = -> Cylinder004
  Edges = 1 edges r=1.8: [Edge3]
FEATURE [Part::Fillet] Fillet037
  Base = -> Fillet038
  Edges = 1 edges r=1.8: [Edge2]
  Placement = pos=(-6.4,0,0) rot=(0,0,1;0rad)
FEATURE [Sketcher::SketchObject] Sketch048
  FullyConstrained = true
  sketch-geometry (4):
    g0: LineSegment StartX=-5.1 StartY=-34.18 StartZ=0 EndX=5.1 EndY=-34.18 EndZ=0
    g1: LineSegment StartX=-5.1 StartY=-3.93167e-07 StartZ=0 EndX=-5.1 EndY=-34.18 EndZ=0
    g2: LineSegment StartX=5.1 StartY=-34.18 StartZ=0 EndX=5.1 EndY=-3.93167e-07 EndZ=0
    g3: LineSegment StartX=-5.1 StartY=-3.93167e-07 StartZ=0 EndX=5.1 EndY=-3.93167e-07 EndZ=0
  constraints (10):
    c: Horizontal(g0)
    c: Block(g0)
    c: Coincident(g1,g0)
    c: Vertical(g1)
    c: Coincident(g2,g0)
    c: Vertical(g2)
    c: Coincident(g3,g1)
    c: Coincident(g3,g2)
    c: Horizontal(g3)
    c: Block(g3)
FEATURE [Part::Extrusion] Extrude044
  Base = -> Sketch048
  Dir = (0,0,1)
  DirMode = 2
  FaceMakerClass = Part::FaceMakerBullseye
  LengthFwd = 6.2
  LengthRev = 0
  Solid = true
  Symmetric = false
FEATURE [Part::Fillet] Fillet039
  Base = -> Extrude044
  Edges = 1 edges r=3.09: [Edge7]
FEATURE [Part::Fillet] Fillet040
  Base = -> Fillet039
  Edges = 1 edges r=3.09: [Edge8]
FEATURE [Part::Fillet] Fillet041
  Base = -> Fillet040
  Edges = 1 edges r=3.09: [Edge17]
FEATURE [Part::Fillet] Fillet042  label="removeFromMainToMakeUSBCableHole"
  Base = -> Fillet041
  Edges = 1 edges r=3.09: [Edge10]
  Placement = pos=(-111.4,30,10.9) rot=(0,1,0;1.5708rad)
FEATURE [Part::Cylinder] Cylinder
  Angle = 360
  AttacherType = Attacher::AttachEngine3D
  Height = 17.6
  Placement = pos=(-116.86,-14.05,2.4) rot=(0,0,1;0rad)
  Radius = 8.4
FEATURE [Part::Box] Box080  label="Cube080"
  AttacherType = Attacher::AttachEngine3D
  Height = 20
  Length = 6
  Placement = pos=(-120.65,-16.05,2.4) rot=(0,0,-1;0.349066rad)
  Width = 13.85
FEATURE [Part::Cylinder] Cylinder005
  Angle = 360
  AttacherType = Attacher::AttachEngine3D
  Height = 20
  Placement = pos=(-116.86,-14.05,30) rot=(0,0,1;0rad)
  Radius = 11.06
FEATURE [Part::Box] Box081  label="Cube081"
  AttacherType = Attacher::AttachEngine3D
  Height = 20
  Length = 10
  Placement = pos=(-115.9,-3.3,30) rot=(0,0,-1;0.314159rad)
  Width = 10
FEATURE [App::MeasureDistance] Distance001  label="Distance: 2.40 mm"
  Distance = 2.4
  P1 = (-129.5,-19.3,2.4)
  P2 = (-129.5,-19.3,0)
FEATURE [Part::MultiFuse] Fusion047
  Shapes = -> [Box080,Cylinder]
FEATURE [Part::Cylinder] Cylinder006
  Angle = 360
  AttacherType = Attacher::AttachEngine3D
  Height = 10
  Placement = pos=(-112,-13.1,17) rot=(0,1,0;1.5708rad)
  Radius = 4.4
FEATURE [Part::MultiFuse] Fusion048  label="removeFromMainToCreateHoleForUSBCablePillar"
  Shapes = -> [Fusion047,Cylinder006]
FEATURE [Part::Extrusion] Extrude046
  Base = -> Sketch047
  Dir = (0,0,1)
  DirMode = 2
  FaceMakerClass = Part::FaceMakerBullseye
  LengthFwd = 8
  LengthRev = 0
  Solid = true
  Symmetric = false
FEATURE [App::MeasureDistance] Distance002  label="Distance: 12.20 mm"
  Distance = 12.2
  P1 = (32.7,-36,8)
  P2 = (20.5,-36,8)
FEATURE [Part::Fillet] Fillet
  Base = -> Extrude046
  Edges = 1 edges r=3.9: [Edge12]
FEATURE [Part::Fillet] Fillet048
  Base = -> Fillet
  Edges = 1 edges r=3.9: [Edge8]
FEATURE [Part::Fillet] Fillet049
  Base = -> Fillet048
  Edges = 1 edges r=3.9: [Edge17]
FEATURE [Part::Fillet] Fillet050
  Base = -> Fillet049
  Edges = 1 edges r=3.9: [Edge11]
  Placement = pos=(-55,0,8.3) rot=(1,0,0;0.191986rad)
FEATURE [Part::MultiFuse] Fusion049
  Shapes = -> [Fillet031,Fillet036,Fillet037]
FEATURE [Part::Cut] Cut027
  Base = -> Cylinder005
  Placement = pos=(0,0,-30) rot=(0,0,1;0rad)
  Tool = -> Box081
FEATURE [Sketcher::SketchObject] Sketch049
  FullyConstrained = true
  sketch-geometry (4):
    g0: LineSegment StartX=-5.1 StartY=-34.18 StartZ=0 EndX=5.1 EndY=-34.18 EndZ=0
    g1: LineSegment StartX=-5.1 StartY=-3.93167e-07 StartZ=0 EndX=-5.1 EndY=-34.18 EndZ=0
    g2: LineSegment StartX=5.1 StartY=-34.18 StartZ=0 EndX=5.1 EndY=-3.93167e-07 EndZ=0
    g3: LineSegment StartX=-5.1 StartY=-3.93167e-07 StartZ=0 EndX=5.1 EndY=-3.93167e-07 EndZ=0
  constraints (10):
    c: Horizontal(g0)
    c: Block(g0)
    c: Coincident(g1,g0)
    c: Vertical(g1)
    c: Coincident(g2,g0)
    c: Vertical(g2)
    c: Coincident(g3,g1)
    c: Coincident(g3,g2)
    c: Horizontal(g3)
    c: Block(g3)
FEATURE [Part::Extrusion] Extrude047
  Base = -> Sketch049
  Dir = (0,0,1)
  DirMode = 2
  FaceMakerClass = Part::FaceMakerBullseye
  LengthFwd = 6.2
  LengthRev = 0
  Solid = true
  Symmetric = false
FEATURE [Part::Fillet] Fillet054
  Base = -> Extrude047
  Edges = 1 edges r=3.09: [Edge7]
FEATURE [Part::Fillet] Fillet051
  Base = -> Fillet054
  Edges = 1 edges r=3.09: [Edge8]
FEATURE [Part::Fillet] Fillet052
  Base = -> Fillet051
  Edges = 1 edges r=3.09: [Edge17]
FEATURE [Part::Fillet] Fillet053  label="removeFromMainToMakeUSBCableHole001"
  Base = -> Fillet052
  Edges = 1 edges r=3.09: [Edge10]
  Placement = pos=(-111.4,30,14.9) rot=(0,1,0;1.5708rad)
FEATURE [Sketcher::SketchObject] Sketch050
  FullyConstrained = true
  sketch-geometry (4):
    g0: LineSegment StartX=-5.1 StartY=-34.18 StartZ=0 EndX=5.1 EndY=-34.18 EndZ=0
    g1: LineSegment StartX=-5.1 StartY=-3.93167e-07 StartZ=0 EndX=-5.1 EndY=-34.18 EndZ=0
    g2: LineSegment StartX=5.1 StartY=-34.18 StartZ=0 EndX=5.1 EndY=-3.93167e-07 EndZ=0
    g3: LineSegment StartX=-5.1 StartY=-3.93167e-07 StartZ=0 EndX=5.1 EndY=-3.93167e-07 EndZ=0
  constraints (10):
    c: Horizontal(g0)
    c: Block(g0)
    c: Coincident(g1,g0)
    c: Vertical(g1)
    c: Coincident(g2,g0)
    c: Vertical(g2)
    c: Coincident(g3,g1)
    c: Coincident(g3,g2)
    c: Horizontal(g3)
    c: Block(g3)
FEATURE [Part::Extrusion] Extrude048
  Base = -> Sketch050
  Dir = (0,0,1)
  DirMode = 2
  FaceMakerClass = Part::FaceMakerBullseye
  LengthFwd = 6.2
  LengthRev = 0
  Solid = true
  Symmetric = false
FEATURE [Part::Fillet] Fillet058
  Base = -> Extrude048
  Edges = 1 edges r=3.09: [Edge7]
FEATURE [Part::Fillet] Fillet056
  Base = -> Fillet058
  Edges = 1 edges r=3.09: [Edge8]
FEATURE [Part::Fillet] Fillet055
  Base = -> Fillet056
  Edges = 1 edges r=3.09: [Edge17]
FEATURE [Part::Fillet] Fillet057  label="removeFromMainToMakeUSBCableHole002"
  Base = -> Fillet055
  Edges = 1 edges r=3.09: [Edge10]
  Placement = pos=(-111.4,30,18.4) rot=(0,1,0;1.5708rad)
FEATURE [Part::MultiFuse] Fusion050  label="removeFusion050"
  Shapes = -> [Fillet057,Fillet053,Fillet042]
FEATURE [Part::Box] Box082  label="Cube082"
  AttacherType = Attacher::AttachEngine3D
  Height = 3
  Length = 3
  Placement = pos=(-20,-23.5,17) rot=(0,0,1;0rad)
  Width = 23
FEATURE [Part::Box] Box083  label="Cube083"
  AttacherType = Attacher::AttachEngine3D
  Height = 3
  Length = 3
  Placement = pos=(-40,-23.5,17) rot=(0,0,1;0rad)
  Width = 23
FEATURE [Part::Box] Box086  label="Cube086"
  AttacherType = Attacher::AttachEngine3D
  Height = 8
  Length = 28
  Placement = pos=(-132,-26,0) rot=(0,0,1;0rad)
  Width = 23
FEATURE [Part::Box] Box087  label="Cube087"
  AttacherType = Attacher::AttachEngine3D
  Height = 8
  Length = 12
  Placement = pos=(-98,-26,0) rot=(0,0,1;0rad)
  Width = 23
FEATURE [Part::Box] Box088  label="Cube088"
  AttacherType = Attacher::AttachEngine3D
  Height = 8
  Length = 12
  Placement = pos=(-108,-10,0) rot=(0,0,1;0rad)
  Width = 8
FEATURE [Part::MultiFuse] Fusion051  label="extraStrengthFusion051"
  Shapes = -> [Box087,Box088,Box086]
FEATURE [Part::Fillet] Fillet059
  Base = -> Fusion051
  Edges = 1 edges r=4: [Edge8]
FEATURE [Part::MultiFuse] Fusion052  label="main"
  Shapes = -> [Box083,Box082,Cut017,Extrude001,Fillet059,Revolve]
FEATURE [Part::Cut] Cut028
  Base = -> Fusion052
  Tool = -> Fusion050
FEATURE [Part::Fillet] Fillet060
  Base = -> Cut028
  Edges = 1 edges r=2: [Edge287]
FEATURE [Part::Cut] Cut029
  Base = -> Fillet060
  Tool = -> Fillet050
FEATURE [Part::Cut] Cut030
  Base = -> Cut029
  Tool = -> Fusion049
FEATURE [Part::Cut] Cut031  label="mainCut031"
  Base = -> Cut030
  Tool = -> Fusion037
FEATURE [App::MeasureDistance] Distance003  label="Distance: 69.20 mm"
  Distance = 69.2
  P1 = (-2.5,-29.6975,8.49911)
  P2 = (-71.7,-29.6975,8.49911)
FEATURE [App::MeasureDistance] Distance004  label="Distance: 10.00 mm"
  Distance = 10
  P1 = (-56.7,-29.6975,8.49911)
  P2 = (-46.7,-29.6975,8.49911)
FEATURE [Sketcher::SketchObject] Sketch051
  FullyConstrained = true
  MapMode = 4
  Placement = pos=(0,0,0) rot=(0.57735,0.57735,0.57735;2.0944rad)
  sketch-geometry (14):
    g0: LineSegment StartX=6.08745 StartY=-4.11588 StartZ=0 EndX=6.08745 EndY=-2.11589 EndZ=0
    g1: LineSegment StartX=8.08745 StartY=1.38411 StartZ=0 EndX=8.08745 EndY=-1.11589 EndZ=0
    g2: ArcOfCircle CenterX=7.08745 CenterY=-1.11589 CenterZ=0 NormalX=0 NormalY=0 NormalZ=1 AngleXU=0 Radius=1 StartAngle=4.71239 EndAngle=6.28319
    g3: LineSegment StartX=6.08745 StartY=-2.11589 StartZ=0 EndX=7.08745 EndY=-2.11589 EndZ=0
    g4: LineSegment StartX=6.08745 StartY=-4.11588 StartZ=0 EndX=7.08745 EndY=-4.11588 EndZ=0
    g5: ArcOfCircle CenterX=7.08745 CenterY=-1.11589 CenterZ=0 NormalX=0 NormalY=0 NormalZ=1 AngleXU=0 Radius=3 StartAngle=4.71239 EndAngle=6.28319
    g6: ArcOfCircle CenterX=7.08745 CenterY=1.38411 CenterZ=0 NormalX=0 NormalY=0 NormalZ=1 AngleXU=0 Radius=1 StartAngle=5.35e-14 EndAngle=1.5708
    g7: LineSegment StartX=10.0875 StartY=-1.11588 StartZ=0 EndX=10.0875 EndY=1.38411 EndZ=0
    g8: ArcOfCircle CenterX=7.08745 CenterY=1.38411 CenterZ=0 NormalX=0 NormalY=0 NormalZ=1 AngleXU=0 Radius=3 StartAngle=3.57e-14 EndAngle=1.5708
    g9: ArcOfCircle CenterX=4.58745 CenterY=1.38412 CenterZ=0 NormalX=0 NormalY=0 NormalZ=1 AngleXU=0 Radius=1 StartAngle=1.57081 EndAngle=3.14159
    g10: LineSegment StartX=4.58744 StartY=2.38411 StartZ=0 EndX=7.08745 EndY=2.38411 EndZ=0
    g11: LineSegment StartX=4.58745 StartY=4.38411 StartZ=0 EndX=7.08745 EndY=4.38411 EndZ=0
    g12: ArcOfCircle CenterX=4.58745 CenterY=5.38411 CenterZ=0 NormalX=0 NormalY=0 NormalZ=1 AngleXU=0 Radius=1 StartAngle=3.14159 EndAngle=4.71239
    g13: LineSegment StartX=3.58745 StartY=5.38411 StartZ=0 EndX=3.58745 EndY=1.38411 EndZ=0
  constraints (33):
    c: Vertical(g0)
    c: Block(g0)
    c: Block(g1)
    c: Coincident(g2,g1)
    c: Coincident(g3,g0)
    c: Coincident(g3,g2)
    c: Horizontal(g3)
    c: Block(g2)
    c: Coincident(g4,g0)
    c: Horizontal(g4)
    c: Coincident(g5,g2)
    c: Block(g5)
    c: Block(g4)
    c: Coincident(g6,g1)
    c: Block(g6)
    c: Coincident(g7,g5)
    c: Vertical(g7)
    c: Coincident(g8,g6)
    c: Block(g8)
    c: Block(g7)
    c: Coincident(g10,g9)
    c: Coincident(g10,g6)
    c: Horizontal(g10)
    c: Block(g10)
    c: Block(g9)
    c: Coincident(g11,g8)
    c: Horizontal(g11)
    c: Block(g12)
    c: Block(g11)
    c: Coincident(g13,g12)
    c: Coincident(g13,g9)
    c: Vertical(g13)
    c: Tangent(g13,g9)
FEATURE [Part::Extrusion] Extrude049
  Base = -> Sketch051
  Dir = (1,0,0)
  DirMode = 2
  FaceMakerClass = Part::FaceMakerBullseye
  LengthFwd = 10
  LengthRev = 0
  Placement = pos=(-34.55,-22.61,4.115) rot=(0,0,1;3.14159rad)
  Solid = true
  Symmetric = false
